# Revit family: LLHV
name_source: partatom
category: Lighting Fixtures
revit_build: Autodesk Revit Architecture 2012 (Build: 20110309_2315(x64)
units: mm (PartAtom-declared; Revit-internal decimal feet)

## types (2) — shared parameters
Apparent Load = 0 VA
Backbox = White
Color Filter = 16777215
Default Elevation = 1219 mm
Description = VersaBay® LED combines powerful, high light output LED technology with remarkable energy savings for a quick return on investment.
Dimming Lamp Color Temperature Shift = <None>
Driver = 0-10V Dimming
Emit from Line Length = 305 mm
Glass = White Glass
Lamp = LED
Length = 1219 mm
Lumen Output = High Lumen
Manufacturer = Columbia Lighting
Manufacturer Fax = (866)-898-1065
Model = LLHV
Nominal Watts = 236 W
Product Documentation Link = http://www.columbialighting.com
Product Page URL = http://www.columbialighting.com
Tilt Angle = -90.00°
URL = http://www.columbialighting.com
Uplight = Solid Top
Voltage = 120 V

## per-type parameters (varying)
| type | Photometric Web File | Reflector |
| LLHV4-50H-NST-EDU | LLHV4-50H-NST-EDU.ies | Narrow Distribution |
| LLHV4-50H-WST-EDU | LLHV4-50H-WST-EDU.ies | Wide Distribution |

## geometry (parser evidence)
native form markers: Sweep x4
no freeform markers — native parametric forms only
